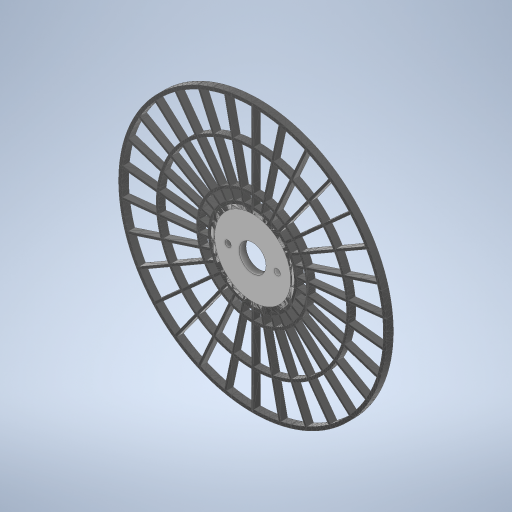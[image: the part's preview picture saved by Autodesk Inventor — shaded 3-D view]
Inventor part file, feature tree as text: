
AUTODESK INVENTOR PART (.ipt)
format: ipt  version: 2024 (Build 280153000, 153)  size: 393,216 bytes
history: native  units: mm
features: other x2, extrude x2, sketch x2, projected_geometry x1
ambient origin geometry x8: Origin, YZ Plane, XZ Plane, XY Plane, X Axis, Y Axis, Z Axis, Center Point
bodies: Solid1 (feature_tree)
feature tree (7):
  other  "protection_cover_back"
  extrude  "Extrusion1"  Depth=3.0mm
  extrude  "Extrusion2"  Depth=3.0mm
  sketch  "Sketch1"  dims[d0=3.0mm d1=0.0mm d2=32.0mm]
  sketch  "Sketch2"  dims[d3=12.0mm d4=2.75mm d5=22.0mm d6=3.0mm d7=0.0mm]
  projected_geometry  "Projected Loop1"
  other  "MeshFeature1"
